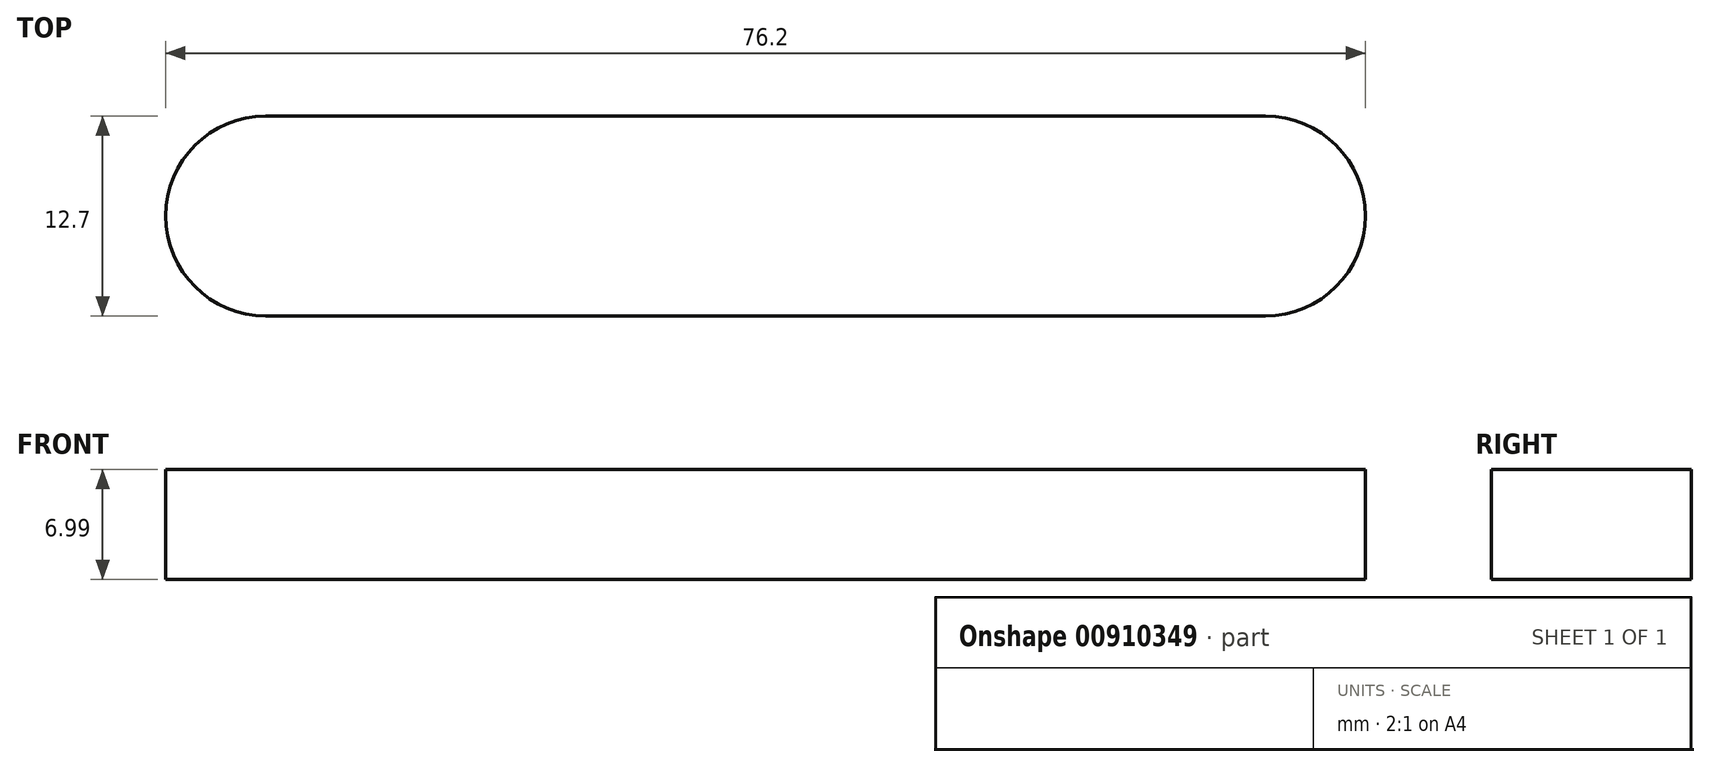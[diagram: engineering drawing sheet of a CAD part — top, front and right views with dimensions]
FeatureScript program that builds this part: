
annotation { "Feature Type Name" : "Feature", "Feature Type Description" : "" }
export const myFeature = defineFeature(function(context is Context, id is Id, definition is map)
    precondition{}
    {
        {
            var Q0;
            Q0=qCreatedBy(makeId("Top.planeOp"),FACE);
            var sketch = newSketch(context, id + "F0", { "sketchPlane" : qUnion([Q0])});
            skLineSegment(sketch, "E0.bottom", {"start": v(31.75, 6.35) * mm, "end": v(-31.75, 6.35) * mm});
            skLineSegment(sketch, "E0.top", {"start": v(31.75, -6.35) * mm, "end": v(-31.75, -6.35) * mm});
            skLineSegment(sketch, "E0.left", {"start": v(31.75, 6.35) * mm, "end": v(31.75, -6.35) * mm, "construction": true});
            skLineSegment(sketch, "E0.right", {"start": v(-31.75, 6.35) * mm, "end": v(-31.75, -6.35) * mm, "construction": true});
            skPoint(sketch, "E0.middle", {"position": v(0, 0) * mm});
            skArc(sketch, "E1", {"start": v(31.75, -6.35) * mm, "mid": v(38.1, 0) * mm, "end": v(31.75, 6.35) * mm});
            skArc(sketch, "E2", {"start": v(-31.75, 6.35) * mm, "mid": v(-38.1, 0) * mm, "end": v(-31.75, -6.35) * mm});
            skSolve(sketch);
        }
        {
            var Q0;
            Q0 = qSketchRegion(id + "F0", true);
            extrude(context, id + "F1", {"entities" : qUnion([Q0]), "depth" : 7 * mm, "offsetDistance" : 25.4 * mm});
        }
    });
